# Revit family: Plumbing_Drainage_Menzies-Metal_Clamp-Tite_Copper-Drain_Small-Bowl (1)
name_source: partatom
category: Plumbing Fixtures
revit_build: Autodesk Revit 2018 (Build: 20170223_1515(x64)
units: mm (PartAtom-declared; Revit-internal decimal feet)

## family parameters
Cut with Voids When Loaded = No
Host = Face
OmniClass Number = 23.70.50.21.24.11
OmniClass Title = Roof Waste Water Drains
Part Type = Normal
Room Calculation Point = No
Round Connector Dimension = Use Diameter
Shared = No

## types (3) — shared parameters
Assembly Code = D2040200
Default Elevation = 4' - 0"
Description = Clamp-Tite Spun Copper Drain Small Bowl
Drain Flow = 0 GPM
Edition number = 1
Manufacturer = Menzies Metal Products
Pipe Length = 0' - 10 7/8"
Pipe Length Note = Longer pipes available.  Pipes can be field cut to the desired length.
Product Guid = 76b443be-9627-40ef-aff5-f8327594387a
Product Material = Metal - Menzies Metal Products - Copper
Product data url = https://bimobject.com
URL = https://www.menzies-metal.com

## per-type parameters (varying)
| type | Model | Weight |
| 2" | 300-3150 | 4.05 lbf |
| 3" | 300-3155 | 4.95 lbf |
| 4" | 300-3160 | 5.50 lbf |

note: column(s) folded — value = type name in every type: Pipe Diameter

## geometry (parser evidence)
native form markers: Sweep x3
no freeform markers — native parametric forms only
